# Revit family: QF_Brema_G280W_G510W_TM250W_TM450W_cat
name_source: partatom
category: Specialty Equipment
revit_build: Autodesk Revit MEP 2012 (Build: 20110916_2132(x64)
units: mm (PartAtom-declared; Revit-internal decimal feet)

## types (4) — shared parameters
Assembly Code = E1090320
BTUH = 0 W
Cold Water Connection Height = 130 mm  [stored 0.426509 ft]
Cold Water Maximum Pressure = 6.0 bar
Cold Water Minimum Pressure = 1.0 bar
Cold Water Size = 1"
Cold Water Size Radius = 1/2"
Conn Conduit = Yes
Cycle = 50 Hz
Depth = 569 mm  [stored 1.8668 ft]
Description = AUTOMATIC ICE CUBE MAKER WATER COOLED
Elec Conn Connection Height = 290 mm  [stored 0.951444 ft]
FL Amps = 0 A
Height = 695 mm  [stored 2.28018 ft]
Indirect Waste Connection Height = 65 mm  [stored 0.213255 ft]
Indirect Waste Radius = 1/2"
Indirect Waste Size = 1"
Manufacturer = BREMA
Min Ckt Ampacity = 0 A
Phase = 1
Refrigerant Type = R404A
URL = www.bremaice.it
Volts = 230 V
Width = 560 mm  [stored 1.83727 ft]

## per-type parameters (varying)
| type | Apparent Power | Max Overcurrent Protection | Watts | Weight |
| G280W | 1050 VA | 16 A | 1050 W | 83 kg |
| G510W | 1700 VA | 16 A | 1700 W | 102 kg |
| TM250W | 1050 VA | 10 A | 1050 W | 83 kg |
| TM450W | 1700 VA | 10 A | 1700 W | 102 kg |

note: column(s) folded — value = type name in every type: Model

note: [stored X ft] marks values corroborated as IEEE doubles in the binary element streams (Revit-internal decimal feet)

## geometry (parser evidence)
native form markers: Blend x7, Sweep x2
no freeform markers — native parametric forms only
